# Revit family: ROSENBERG_EKAD
name_source: partatom
category: Wyposażenie mechaniczne
revit_build: Autodesk Revit MEP 2016 (Build: 20150220_1215(x64)
units: mm (PartAtom-declared; Revit-internal decimal feet)

## family parameters
Numer OmniClass = 23.75.00.00
Oparty na płaszczyźnie roboczej = Nie
Punkt obliczania pomieszczeń = Nie
Tnij formami wycięć po wczytaniu = Nie
Typ części = Dzieli na
Tytuł OmniClass = Climate Control (HVAC)
Współdzielony = Tak
Wymiar okrągłego złącza = Użyj średnicy
Zawsze pionowo = Tak

## types (17) — shared parameters
Częstotliwość pracy = 50 Hz
Materiał = <Wg kategorii>
Napięcie znamionowe = 400 V
Opis = Wentylator kanałowy EKA
Producent = Rosenberg
param.otw = 60 mm
param.went.podstawa2R = 160 mm  [stored 0.524934 ft]
param.went.podstawaR = 250 mm  [stored 0.82021 ft]
param.went.ram = 180 mm  [stored 0.590551 ft]
zero-valued in all types: param.os.went

## per-type parameters (varying)
| type | Charakterystyka pracy | Klasa szczelności | Masa | Moc znamionowa | Numer katalogowy | Prąd znamionowy | Szerokość przyłącza | URL | Wysokość przyłącza | param.Długość | param.Szerokość | param.Wysokość | param.szer.ogol | param.wentylator |
| EKAD 200-4 Ex | https://rosenberg.pl | IP44 | 12.30 kg | 290 W | D80-20070 | 1 A | 400 mm  [stored 1.31234 ft] | https://rosenberg.pl | 200 mm  [stored 0.656168 ft] | 445 mm  [stored 1.45997 ft] | 400 mm  [stored 1.31234 ft] | 200 mm  [stored 0.656168 ft] | 440 mm | 240 mm  [stored 0.787402 ft] |
| EKAD 225-4 Ex | https://rosenberg.pl | IP44 | 13.00 kg | 540 W | D80-22571 | 1 A | 500 mm  [stored 1.64042 ft] | https://rosenberg.pl | 250 mm  [stored 0.82021 ft] | 530 mm | 500 mm  [stored 1.64042 ft] | 250 mm  [stored 0.82021 ft] | 540 mm | 290 mm |
| EKAD 250-4 Ex | https://rosenberg.pl | IP44 | 22.00 kg | 750 W | D80-25071 | 1 A | 500 mm  [stored 1.64042 ft] | https://rosenberg.pl | 300 mm | 560 mm | 500 mm  [stored 1.64042 ft] | 300 mm | 540 mm | 340 mm |
| EKAD 280-4 Ex | http://rosenberg.pl | IP44 | 36.50 kg | 1500 W | D80-28072 | 3 A | 600 mm | http://rosenberg.pl | 300 mm | 680 mm | 600 mm | 300 mm | 640 mm  [stored 2.09974 ft] | 340 mm |
| EKAD 280-6 Ex | https://rosenberg.pl | IP44 | 28.00 kg | 530 W | D80-28073 | 1 A | 600 mm | https://rosenberg.pl | 300 mm | 680 mm | 600 mm | 300 mm | 640 mm  [stored 2.09974 ft] | 340 mm |
| EKAD 315-4 Ex | https://rosenberg.pl | IP44 | 46.50 kg | 2000 W | D80-31574 | 4 A | 600 mm | https://rosenberg.pl | 350 mm  [stored 1.14829 ft] | 700 mm | 600 mm | 350 mm  [stored 1.14829 ft] | 640 mm  [stored 2.09974 ft] | 390 mm |
| EKAD 315-6 Ex | https://rosenberg.pl | IP44 | 46.50 kg | 710 W | D80-31573 | 1 A | 600 mm | https://rosenberg.pl | 350 mm  [stored 1.14829 ft] | 700 mm | 600 mm | 350 mm  [stored 1.14829 ft] | 640 mm  [stored 2.09974 ft] | 390 mm |
| EKAD 355-6 Ex | https://rosenberg.pl | IP44 | 55.50 kg | 1350 W | D80-35571 | 2 A | 700 mm | https://rosenberg.pl | 400 mm  [stored 1.31234 ft] | 780 mm | 700 mm | 400 mm  [stored 1.31234 ft] | 740 mm | 440 mm |
| EKAD 280-4.6FA | https://rosenberg.pl | IP54 | 35.00 kg | 1090 W | D00-28059 | 2 A | 600 mm | https://rosenberg.pl | 300 mm | 680 mm | 600 mm | 300 mm | 640 mm  [stored 2.09974 ft] | 340 mm |
| EKAD 315-4.6HF | https://rosenberg.pl | IP54 | 44.00 kg | 1950 W | D00-31550 | 4 A | 600 mm | https://rosenberg.pl | 350 mm  [stored 1.14829 ft] | 700 mm | 600 mm | 350 mm  [stored 1.14829 ft] | 640 mm  [stored 2.09974 ft] | 390 mm |
| EKAD 400-4.7NA | https://rosenberg.pl | IP54 | 86.00 kg | 4100 W | D00-40050 | 7 A | 800 mm | https://rosenberg.pl | 500 mm  [stored 1.64042 ft] | 880 mm | 800 mm | 500 mm  [stored 1.64042 ft] | 840 mm | 540 mm |
| EKAD 400-6.7KF | https://rosenberg.pl | IP54 | 82.00 kg | 2750 W | D00-40051 | 5 A | 800 mm | https://rosenberg.pl | 500 mm  [stored 1.64042 ft] | 880 mm | 800 mm | 500 mm  [stored 1.64042 ft] | 840 mm | 540 mm |
| EKAD 400-8.7HA | https://rosenberg.pl | IP54 | 75.00 kg | 1400 W | D00-40052 | 3 A | 800 mm | https://rosenberg.pl | 500 mm  [stored 1.64042 ft] | 880 mm | 800 mm | 500 mm  [stored 1.64042 ft] | 840 mm | 540 mm |
| EKAD 450-6.7NA | https://rosenberg.pl | IP54 | 97.00 kg | 3350 W | D00-45050 | 7 A | 900 mm | https://rosenberg.pl | 500 mm  [stored 1.64042 ft] | 1035 mm | 900 mm | 500 mm  [stored 1.64042 ft] | 940 mm | 540 mm |
| EKAD 450-8.7KF | https://rosenberg.pl | IP54 | 85.00 kg | 1930 W | D00-45051 | 4 A | 900 mm | https://rosenberg.pl | 500 mm  [stored 1.64042 ft] | 1035 mm | 900 mm | 500 mm  [stored 1.64042 ft] | 940 mm | 540 mm |
| EKAD 355-4.7KF | https://rosenberg.pl | IP54 | 61.00 kg | 3350 W | D00-35558 | 6 A | 700 mm | https://rosenberg.pl | 400 mm  [stored 1.31234 ft] | 780 mm | 700 mm | 400 mm  [stored 1.31234 ft] | 740 mm | 440 mm |
| EKAD 250-4.5FA | https://rosenberg.pl | IP54 | 23.00 kg | 760 W | D00-25055 | 1 A | 500 mm  [stored 1.64042 ft] | https://rosenberg.pl | 300 mm | 560 mm | 500 mm  [stored 1.64042 ft] | 300 mm | 540 mm | 340 mm |

note: column(s) folded — value = type name in every type: Model

note: [stored X ft] marks values corroborated as IEEE doubles in the binary element streams (Revit-internal decimal feet)

## geometry (parser evidence)
native form markers: Blend x4, Sweep x5
no freeform markers — native parametric forms only
